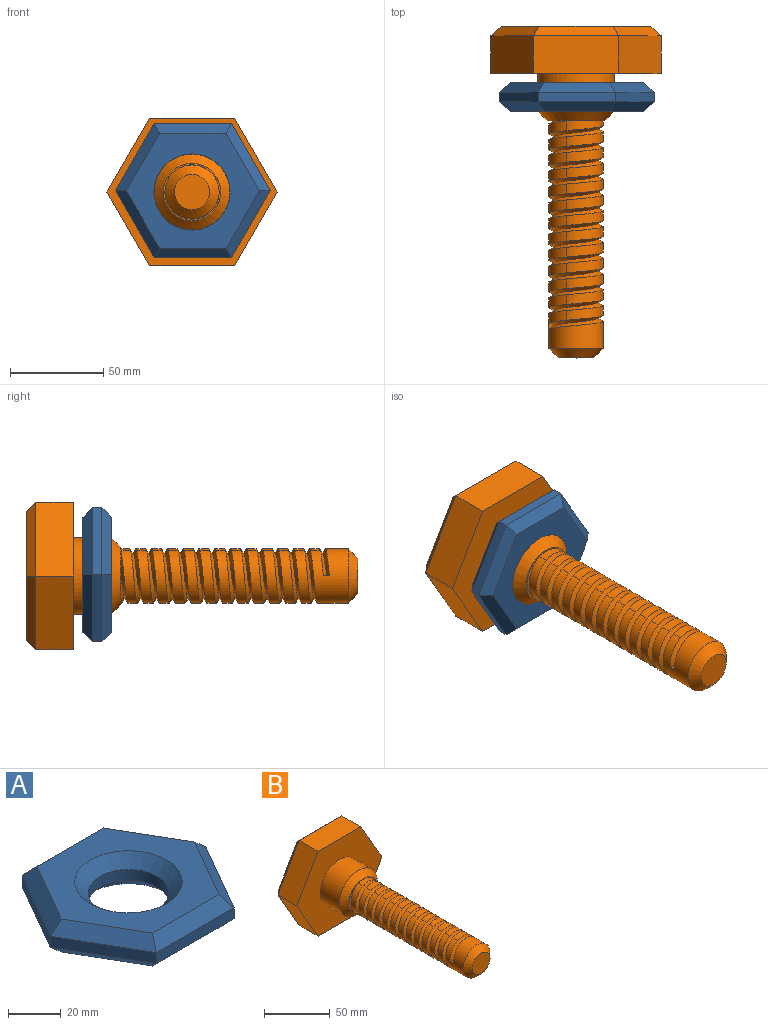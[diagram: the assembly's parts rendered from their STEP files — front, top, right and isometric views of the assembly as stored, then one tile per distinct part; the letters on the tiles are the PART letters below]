
ASSEMBLY  parts=2 mates=1
PART A: 23 faces, bbox 83x71.9x15.2 mm
  f0: plane 35.93x20.74mm, normal (-0.87,0.5,0), area 210.8mm2, adj f1,f5,f15,f22
  f1: plane 35.93x20.74mm, normal (-0.87,-0.5,0), area 210.8mm2, adj f0,f2,f13,f20
  f2: plane 41.49x5.08mm, normal (0,-1,0), area 210.8mm2, adj f1,f3,f11,f18
  f3: plane 35.93x20.74mm, normal (0.87,-0.5,0), area 210.8mm2, adj f2,f4,f10,f17
  f4: plane 35.93x20.74mm, normal (0.87,0.5,0), area 210.8mm2, adj f3,f5,f12,f19
  f5: plane 41.49x5.08mm, normal (0,1,0), area 210.8mm2, adj f0,f4,f14,f21
  f6: plane 71.24x61.7mm, normal (0,0,-1), area 1999.6mm2, adj f16,f17,f18,f19,f20,f21,f22
  f7: plane 71.24x61.7mm, normal (0,0,1), area 1999.6mm2, adj f9,f10,f11,f12,f13,f14,f15
  f8: cylinder r=15.24mm len=30.48mm, axis (0,0,-1), area 486.4mm2, adj f9,f16
  f9: cone r=20.32mm half-angle=45deg, axis (0,0,1), area 802.6mm2, adj f7,f8
  f10: plane 35.93x23.68mm, normal (0.61,-0.35,0.71), area 277mm2, adj f3,f7,f11,f12
  f11: plane 41.49x5.08mm, normal (0,-0.71,0.71), area 277mm2, adj f2,f7,f10,f13
  f12: plane 35.93x23.68mm, normal (0.61,0.35,0.71), area 277mm2, adj f4,f7,f10,f14
  f13: plane 35.93x23.68mm, normal (-0.61,-0.35,0.71), area 277mm2, adj f1,f7,f11,f15
  f14: plane 41.49x5.08mm, normal (0,0.71,0.71), area 277mm2, adj f5,f7,f12,f15
  f15: plane 35.93x23.68mm, normal (-0.61,0.35,0.71), area 277mm2, adj f0,f7,f13,f14
  f16: cone r=15.24mm half-angle=45deg, axis (0,0,-1), area 802.6mm2, adj f6,f8
  f17: plane 35.93x23.68mm, normal (0.61,-0.35,-0.71), area 277mm2, adj f3,f6,f18,f19
  f18: plane 41.49x5.08mm, normal (0,-0.71,-0.71), area 277mm2, adj f2,f6,f17,f20
  f19: plane 35.93x23.68mm, normal (0.61,0.35,-0.71), area 277mm2, adj f4,f6,f17,f21
  f20: plane 35.93x23.68mm, normal (-0.61,-0.35,-0.71), area 277mm2, adj f1,f6,f18,f22
  f21: plane 41.49x5.08mm, normal (0,0.71,-0.71), area 277mm2, adj f5,f6,f19,f22
  f22: plane 35.93x23.68mm, normal (-0.61,0.35,-0.71), area 277mm2, adj f0,f6,f20,f21
PART B: 38 faces, bbox 91.1x177.8x78.9 mm
  f0: plane 39.47x22.79mm, normal (-0.87,0,0.5), area 926mm2, adj f1,f5,f6,f37
  f1: plane 39.47x22.79mm, normal (-0.87,0,-0.5), area 926mm2, adj f0,f2,f6,f35
  f2: plane 45.57x20.32mm, normal (0,0,-1), area 926mm2, adj f1,f3,f6,f33
  f3: plane 39.47x22.79mm, normal (0.87,0,-0.5), area 926mm2, adj f2,f4,f6,f32
  f4: plane 39.47x22.79mm, normal (0.87,0,0.5), area 926mm2, adj f3,f5,f6,f34
  f5: plane 45.57x20.32mm, normal (0,0,1), area 926mm2, adj f0,f4,f6,f36
  f6: plane 91.14x78.93mm, normal (0,-1,0), area 4084.9mm2, adj f0,f1,f2,f3,f4,f5,f8
  f7: plane 79.41x68.77mm, normal (0,1,0), area 4096mm2, adj f32,f33,f34,f35,f36,f37
  f8: cylinder r=20.43mm len=40.85mm, axis (0,1,0), area 2607.9mm2, adj f6,f10
  f9: plane 30.69x30.69mm, normal (0,-1,0), area 78mm2, adj f10,f12,f31
  f10: cone r=15.35mm half-angle=45deg, axis (0,1,0), area 807.4mm2, adj f8,f9
  f11: cylinder r=14.52mm len=29.03mm, axis (0,1,0), area 1409.4mm2, adj f24,f26,f28,f29,f30
  f12: cylinder r=14.52mm len=29.03mm, axis (0,1,0), area 146mm2, adj f9,f13,f29
  f13: cylinder r=14.52mm len=29.03mm, axis (0,1,0), area 474.7mm2, adj f12,f14,f29,f30
  f14: cylinder r=14.52mm len=29.03mm, axis (0,1,0), area 474.7mm2, adj f13,f15,f29,f30
  f15: cylinder r=14.52mm len=29.03mm, axis (0,1,0), area 474.7mm2, adj f14,f16,f29,f30
  f16: cylinder r=14.52mm len=29.03mm, axis (0,1,0), area 474.7mm2, adj f15,f17,f29,f30
  f17: cylinder r=14.52mm len=29.03mm, axis (0,1,0), area 474.7mm2, adj f16,f18,f29,f30
  f18: cylinder r=14.52mm len=29.03mm, axis (0,1,0), area 474.7mm2, adj f17,f19,f29,f30
  f19: cylinder r=14.52mm len=29.03mm, axis (0,1,0), area 474.7mm2, adj f18,f20,f29,f30
  f20: cylinder r=14.52mm len=29.03mm, axis (0,1,0), area 474.7mm2, adj f19,f21,f29,f30
  f21: cylinder r=14.52mm len=29.03mm, axis (0,1,0), area 474.7mm2, adj f20,f22,f29,f30
  f22: cylinder r=14.52mm len=29.03mm, axis (0,1,0), area 474.7mm2, adj f21,f23,f29,f30
  f23: cylinder r=14.52mm len=29.03mm, axis (0,1,0), area 474.7mm2, adj f22,f24,f29,f30
  f24: cylinder r=14.52mm len=29.03mm, axis (0,1,0), area 474.7mm2, adj f11,f23,f29,f30
  f25: plane 18.87x18.87mm, normal (0,-1,0), area 279.7mm2, adj f26
  f26: cone r=9.44mm half-angle=45deg, axis (0,1,0), area 540.6mm2, adj f11,f25
  f27: plane 3.26x2.82mm, normal (0,0,-1), area 4.6mm2, adj f29,f30,f31
  f28: plane 3.26x2.82mm, normal (0,0,1), area 4.6mm2, adj f11,f29,f30
  f29: bspline ~128.63x29.03mm, area 4018.2mm2, adj f11,f12,f13,f14,f15,f16,f17,f18
  f30: bspline ~128.63x29.03mm, area 4044mm2, adj f11,f13,f14,f15,f16,f17,f18,f19
  f31: cylinder r=14.52mm len=29.03mm, axis (0,-1,0), area 594.2mm2, adj f9,f27,f29,f30
  f32: plane 39.47x25.72mm, normal (0.61,0.71,-0.35), area 306.3mm2, adj f3,f7,f33,f34
  f33: plane 45.57x5.08mm, normal (0,0.71,-0.71), area 306.3mm2, adj f2,f7,f32,f35
  f34: plane 39.47x25.72mm, normal (0.61,0.71,0.35), area 306.3mm2, adj f4,f7,f32,f36
  f35: plane 39.47x25.72mm, normal (-0.61,0.71,-0.35), area 306.3mm2, adj f1,f7,f33,f37
  f36: plane 45.57x5.08mm, normal (0,0.71,0.71), area 306.3mm2, adj f5,f7,f34,f37
  f37: plane 39.47x25.72mm, normal (-0.61,0.71,0.35), area 306.3mm2, adj f0,f7,f35,f36
PLACE A rot(axis=(1,0,0),90deg) t=(67.75,-40.26,48.33)mm
PLACE B t=(-66.21,5.46,-11.79)mm fixed
MATE slider A.f8 <-> B.f8  axis (0,-1,0) through (-66.21,-40.26,-11.79)mm
